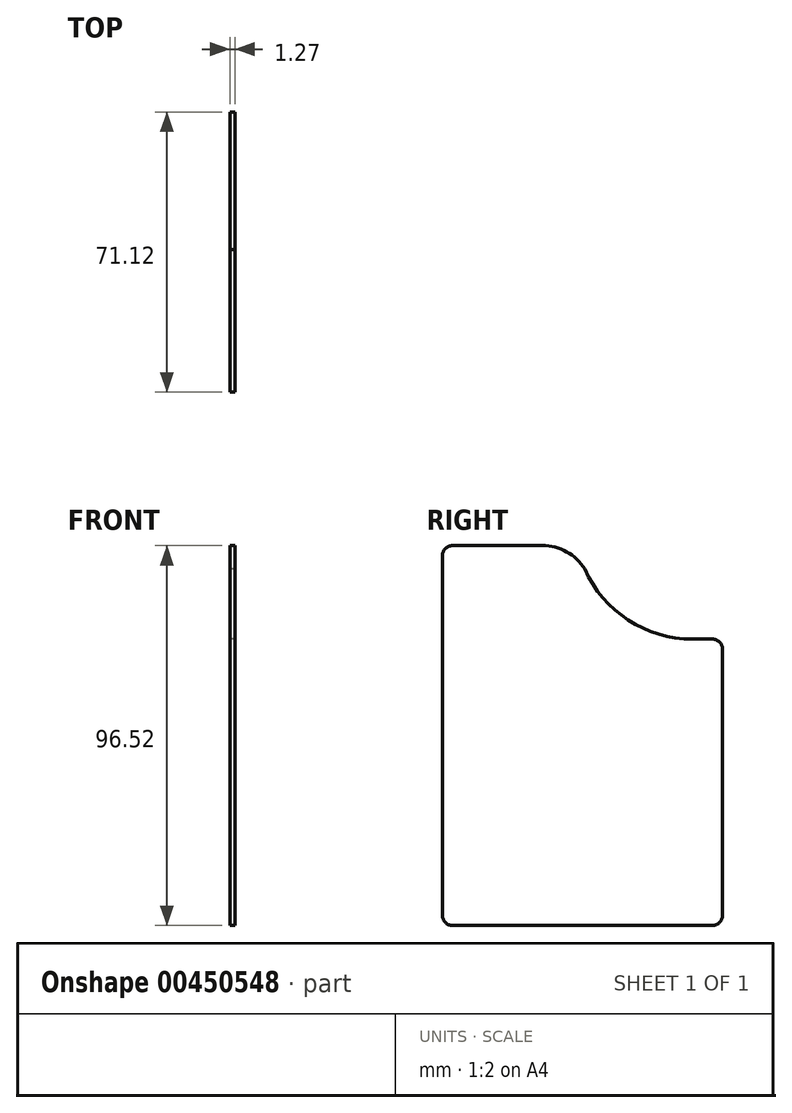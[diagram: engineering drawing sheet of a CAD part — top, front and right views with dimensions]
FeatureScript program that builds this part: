
annotation { "Feature Type Name" : "Feature", "Feature Type Description" : "" }
export const myFeature = defineFeature(function(context is Context, id is Id, definition is map)
    precondition{}
    {
        {
            var Q0;
            Q0=qCreatedBy(makeId("Right.planeOp"),FACE);
            var sketch = newSketch(context, id + "F0", { "sketchPlane" : qUnion([Q0])});
            skLineSegment(sketch, "E0.bottom", {"start": v(-33.88, 42.28) * mm, "end": v(-11.02, 42.28) * mm});
            skLineSegment(sketch, "E0.top", {"start": v(-33.88, -54.24) * mm, "end": v(32.16, -54.24) * mm});
            skLineSegment(sketch, "E0.left", {"start": v(-36.42, 39.74) * mm, "end": v(-36.42, -51.7) * mm});
            skLineSegment(sketch, "E0.right", {"start": v(34.7, 15.98) * mm, "end": v(34.7, -51.7) * mm});
            skPoint(sketch, "E1.visualSharp", {"position": v(-3.32, 42.28) * mm});
            skArc(sketch, "E1.filletArc", {"start": v(-0.27, 36.34) * mm, "mid": v(-4.88, 40.7) * mm, "end": v(-11.02, 42.28) * mm});
            skLineSegment(sketch, "E2", {"start": v(32.16, 18.52) * mm, "end": v(27.08, 18.52) * mm});
            skArc(sketch, "E3", {"start": v(-0.27, 36.34) * mm, "mid": v(10.75, 23.37) * mm, "end": v(27.08, 18.52) * mm});
            skPoint(sketch, "E4.visualSharp", {"position": v(-36.42, -54.24) * mm});
            skArc(sketch, "E4.filletArc", {"start": v(-36.42, -51.7) * mm, "mid": v(-35.68, -53.5) * mm, "end": v(-33.88, -54.24) * mm});
            skPoint(sketch, "E5.visualSharp", {"position": v(34.7, -54.24) * mm});
            skArc(sketch, "E5.filletArc", {"start": v(32.16, -54.24) * mm, "mid": v(33.95, -53.5) * mm, "end": v(34.7, -51.7) * mm});
            skPoint(sketch, "E6.visualSharp", {"position": v(-36.42, 42.28) * mm});
            skArc(sketch, "E6.filletArc", {"start": v(-33.88, 42.28) * mm, "mid": v(-35.68, 41.53) * mm, "end": v(-36.42, 39.74) * mm});
            skPoint(sketch, "E7.visualSharp", {"position": v(34.7, 18.52) * mm});
            skArc(sketch, "E7.filletArc", {"start": v(34.7, 15.98) * mm, "mid": v(33.95, 17.77) * mm, "end": v(32.16, 18.52) * mm});
            skLineSegment(sketch, "E8", {"start": v(-25, 10.53) * mm, "end": v(23.27, 0.37) * mm});
            skSolve(sketch);
        }
        {
            var Q0;
            Q0=makeQuery(id+"F0.imprint","IMPRINT",FACE,{"disambiguationData":[TD([[makeQuery(id+"F0.imprint","IMPRINT",EDGE,{"derivedFrom":sQuery(id+"F0.wireOp",EDGE,"E0.bottom")}),-1.0]])]});
            extrude(context, id + "F1", {"entities" : qUnion([Q0]), "depth" : 1.27 * mm});
        }
    });
